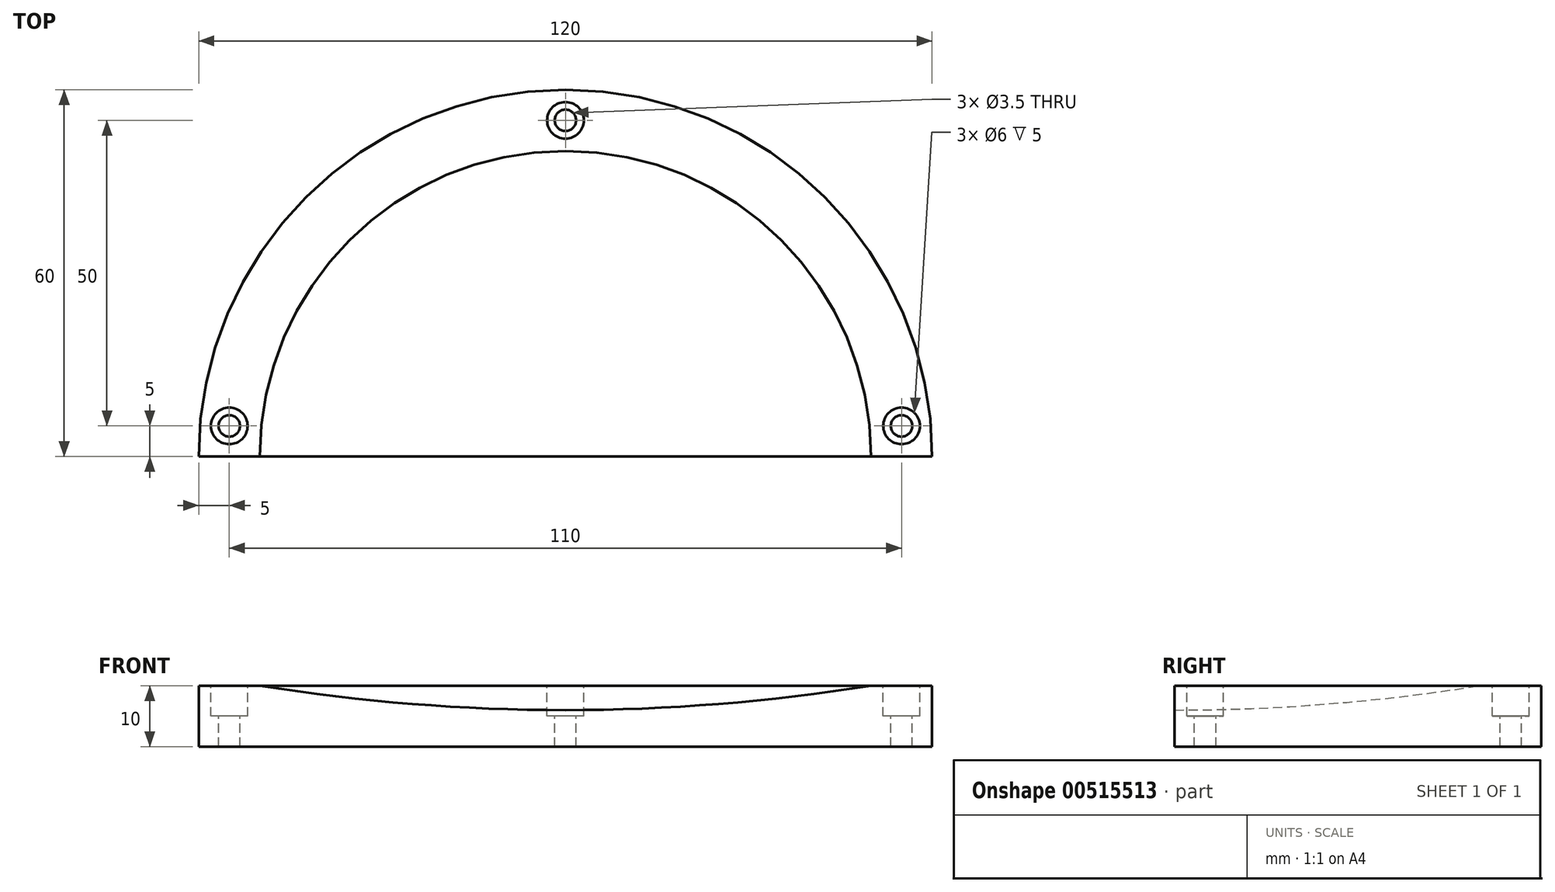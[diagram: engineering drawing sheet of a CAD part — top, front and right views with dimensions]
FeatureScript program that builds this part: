
annotation { "Feature Type Name" : "Feature", "Feature Type Description" : "" }
export const myFeature = defineFeature(function(context is Context, id is Id, definition is map)
    precondition{}
    {
        {
            var Q0;
            Q0=qCreatedBy(makeId("Top.planeOp"),FACE);
            var sketch = newSketch(context, id + "F0", { "sketchPlane" : qUnion([Q0])});
            skCircle(sketch, "E0", {"center": v(0, 0) * mm, "radius": 60 * mm});
            skLineSegment(sketch, "E1", {"start": v(60, 0) * mm, "end": v(-60, 0) * mm});
            skSolve(sketch);
        }
        {
            var Q0;
            {var subQ0=sQuery(id+"F0.wireOp",EDGE,"E1");Q0=makeQuery(id+"F0.imprint","IMPRINT",FACE,{"disambiguationData":[TD([[makeQuery(id+"F0.imprint","IMPRINT",EDGE,{"derivedFrom":subQ0}),-1.0]])]});}
            extrude(context, id + "F1", {"entities" : qUnion([Q0]), "depth" : 10 * mm, "offsetDistance" : 25 * mm});
        }
        {
            var Q0;
            Q0=makeQuery(id+"F1.opExtrude","SWEPT_FACE",FACE,{"disambiguationData":[OSD([sQuery(id+"F0.wireOp",EDGE,"E1")])]});
            var sketch = newSketch(context, id + "F2", { "sketchPlane" : qUnion([Q0])});
            skPoint(sketch, "E2", {"position": v(-50, 10) * mm});
            skPoint(sketch, "E3", {"position": v(50, 10) * mm});
            skLineSegment(sketch, "E4", {"start": v(0, 0) * mm, "end": v(0, 6) * mm});
            skArc(sketch, "E5", {"start": v(-50, 10) * mm, "mid": v(0, 6) * mm, "end": v(50, 10) * mm});
            skLineSegment(sketch, "E6", {"start": v(0, 6) * mm, "end": v(0, 10) * mm});
            skSolve(sketch);
        }
        {
            var Q0;
            {var subQ0=sQuery(id+"F2.wireOp",EDGE,"E6");Q0=makeQuery(id+"F2.imprint","IMPRINT",FACE,{"disambiguationData":[TD([[makeQuery(id+"F2.imprint","IMPRINT",EDGE,{"derivedFrom":subQ0}),1.0]])]});}
            var Q1;
            Q1=sQuery(id+"F2.wireOp",EDGE,"E6");
            revolve(context, id + "F3", {"operationType" : NewBodyOperationType.REMOVE, "entities" : qUnion([Q0]), "axis" : qUnion([Q1]), "revolveType" : RevolveType.FULL});
        }
        {
            var Q0;
            Q0=makeQuery(id+"F1.opExtrude","CAP_FACE",FACE,{"disambiguationData":[OSD([sQuery(id+"F0.wireOp",EDGE,"E0"),sQuery(id+"F0.wireOp",EDGE,"E1")])],"isStart":false});
            var sketch = newSketch(context, id + "F4", { "sketchPlane" : qUnion([Q0])});
            skCircle(sketch, "E7", {"center": v(0, 55) * mm, "radius": 1.75 * mm});
            skCircle(sketch, "E8", {"center": v(-55, 5) * mm, "radius": 1.75 * mm});
            skPoint(sketch, "E8.centerSnap0", {"position": v(-55, 0) * mm});
            skCircle(sketch, "E9", {"center": v(55, 5) * mm, "radius": 1.75 * mm});
            skSolve(sketch);
        }
        {
            var Q0;
            Q0 = qSketchRegion(id + "F4", true);
            extrude(context, id + "F5", {"entities" : qUnion([Q0]), "operationType" : NewBodyOperationType.REMOVE, "oppositeDirection" : true, "depth" : 25 * mm, "offsetDistance" : 25 * mm});
        }
        {
            var Q0;
            Q0=makeQuery(id+"F1.opExtrude","CAP_FACE",FACE,{"disambiguationData":[OSD([sQuery(id+"F0.wireOp",EDGE,"E0"),sQuery(id+"F0.wireOp",EDGE,"E1")])],"isStart":false});
            var sketch = newSketch(context, id + "F6", { "sketchPlane" : qUnion([Q0])});
            skCircle(sketch, "E10", {"center": v(55, 5) * mm, "radius": 3 * mm});
            skCircle(sketch, "E11", {"center": v(0, 55) * mm, "radius": 3 * mm});
            skCircle(sketch, "E12", {"center": v(-55, 5) * mm, "radius": 3 * mm});
            skSolve(sketch);
        }
        {
            var Q0;
            Q0 = qSketchRegion(id + "F6", true);
            extrude(context, id + "F7", {"entities" : qUnion([Q0]), "operationType" : NewBodyOperationType.REMOVE, "oppositeDirection" : true, "depth" : 5 * mm, "offsetDistance" : 25 * mm});
        }
    });
